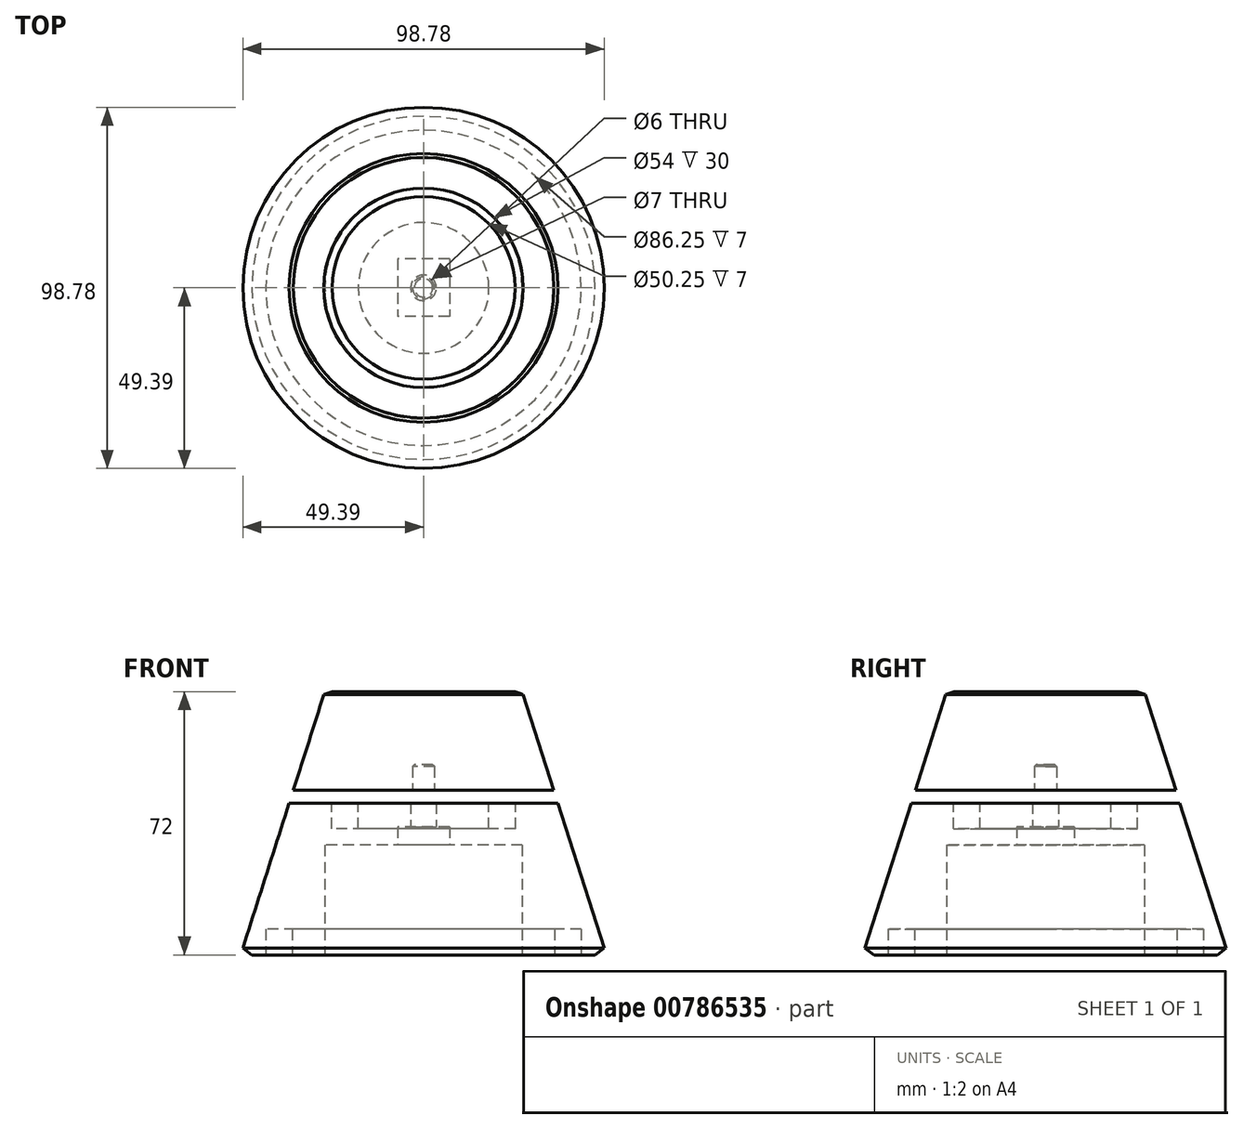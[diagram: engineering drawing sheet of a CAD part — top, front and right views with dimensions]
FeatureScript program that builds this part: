
annotation { "Feature Type Name" : "Feature", "Feature Type Description" : "" }
export const myFeature = defineFeature(function(context is Context, id is Id, definition is map)
    precondition{}
    {
        {
            var Q0;
            Q0=qCreatedBy(makeId("Top.planeOp"),FACE);
            var sketch = newSketch(context, id + "F0", { "sketchPlane" : qUnion([Q0])});
            skCircle(sketch, "E0", {"center": v(0, 0) * mm, "radius": 50 * mm});
            skSolve(sketch);
        }
        {
            var Q0;
            Q0 = qSketchRegion(id + "F0", true);
            extrude(context, id + "F1", {"entities" : qUnion([Q0]), "depth" : 72 * mm, "offsetDistance" : 25 * mm});
        }
        {
            var Q0;
            Q0=makeQuery(id+"F1.opExtrude","CAP_EDGE",EDGE,{"disambiguationData":[OSD([sQuery(id+"F0.wireOp",EDGE,"E0")])],"isStart":false});
            chamfer(context, id + "F2", {"entities" : qUnion([Q0]), "chamferType" : ChamferType.TWO_OFFSETS, "width1" : 23 * mm, "oppositeDirection" : false, "width2" : 72 * mm, "tangentPropagation" : true});
        }
        {
            var Q0;
            {var subQ0=sQuery(id+"F0.wireOp",EDGE,"E0");Q0=makeQuery(id+"F2.opChamfer","BLEND_EDGE",EDGE,{"blendedFrom":[makeQuery(id+"F1.opExtrude","CAP_EDGE",EDGE,{"disambiguationData":[OSD([subQ0])],"isStart":false}),makeQuery(id+"F1.opExtrude","CAP_FACE",FACE,{"disambiguationData":[OSD([subQ0])],"isStart":true})],"blendedInto":[makeQuery(id+"F1.opExtrude","CAP_FACE",FACE,{"disambiguationData":[OSD([subQ0])],"isStart":true})]});}
            chamfer(context, id + "F3", {"entities" : qUnion([Q0]), "chamferType" : ChamferType.OFFSET_ANGLE, "width" : 2 * mm, "oppositeDirection" : false, "angle" : 70 * degree, "tangentPropagation" : true});
        }
        {
            var Q0;
            {var subQ0=sQuery(id+"F0.wireOp",EDGE,"E0");Q0=makeQuery(id+"F2.opChamfer","BLEND_EDGE",EDGE,{"blendedFrom":[makeQuery(id+"F1.opExtrude","CAP_EDGE",EDGE,{"disambiguationData":[OSD([subQ0])],"isStart":false}),makeQuery(id+"F1.opExtrude","CAP_FACE",FACE,{"disambiguationData":[OSD([subQ0])],"isStart":false})],"blendedInto":[makeQuery(id+"F1.opExtrude","CAP_FACE",FACE,{"disambiguationData":[OSD([subQ0])],"isStart":false})]});}
            chamfer(context, id + "F4", {"entities" : qUnion([Q0]), "chamferType" : ChamferType.OFFSET_ANGLE, "width" : 2 * mm, "oppositeDirection" : false, "angle" : 20 * degree, "tangentPropagation" : true});
        }
        {
            var Q0;
            Q0=qCreatedBy(makeId("Top.planeOp"),FACE);
            var sketch = newSketch(context, id + "F5", { "sketchPlane" : qUnion([Q0])});
            skCircle(sketch, "E1", {"center": v(0, 0) * mm, "radius": 27 * mm});
            skSolve(sketch);
        }
        {
            var Q0;
            Q0 = qSketchRegion(id + "F5", true);
            extrude(context, id + "F6", {"entities" : qUnion([Q0]), "operationType" : NewBodyOperationType.REMOVE, "depth" : 30 * mm, "offsetDistance" : 25 * mm});
        }
        {
            var Q0;
            Q0=makeQuery(id+"F6.boolean.opBoolean","COPY",FACE,{"derivedFrom":makeQuery(id+"F6.opExtrude","CAP_FACE",FACE,{"disambiguationData":[OSD([sQuery(id+"F5.wireOp",EDGE,"E1")])],"isStart":false})});
            var sketch = newSketch(context, id + "F7", { "sketchPlane" : qUnion([Q0])});
            skLineSegment(sketch, "E2.bottom", {"start": v(7.12, -7.88) * mm, "end": v(-7.13, -7.88) * mm});
            skLineSegment(sketch, "E2.top", {"start": v(7.12, 7.88) * mm, "end": v(-7.12, 7.87) * mm});
            skLineSegment(sketch, "E2.left", {"start": v(7.12, -7.88) * mm, "end": v(7.12, 7.88) * mm});
            skLineSegment(sketch, "E2.right", {"start": v(-7.13, -7.88) * mm, "end": v(-7.12, 7.87) * mm});
            skPoint(sketch, "E2.middle", {"position": v(0, 0) * mm});
            skSolve(sketch);
        }
        {
            var Q0;
            Q0 = qSketchRegion(id + "F7", true);
            var Q1;
            Q1=sQuery(id+"F7.wireOp",EDGE,"nhaoerKo-kfoO-m88x-1wRI-986FIBOQnDxg");
            extrude(context, id + "F8", {"entities" : qUnion([Q0]), "operationType" : NewBodyOperationType.REMOVE, "surfaceEntities" : qUnion([Q1]), "oppositeDirection" : true, "depth" : 5 * mm, "offsetDistance" : 25 * mm});
        }
        {
            var Q0;
            Q0=makeQuery(id+"F5.imprint","IMPRINT",FACE,{"disambiguationData":[TD([[makeQuery(id+"F5.imprint","IMPRINT",EDGE,{"derivedFrom":sQuery(id+"F5.wireOp",EDGE,"E1")}),1.0]])]});
            var sketch = newSketch(context, id + "F9", { "sketchPlane" : qUnion([Q0])});
            skCircle(sketch, "E3", {"center": v(0, 0) * mm, "radius": 3.5 * mm});
            skSolve(sketch);
        }
        {
            var Q0;
            Q0 = qSketchRegion(id + "F9", true);
            extrude(context, id + "F10", {"entities" : qUnion([Q0]), "operationType" : NewBodyOperationType.REMOVE, "depth" : 41.5 * mm, "offsetDistance" : 25 * mm});
        }
        {
            var Q0;
            Q0=makeQuery(id+"F0.imprint","IMPRINT",FACE,{"disambiguationData":[TD([[makeQuery(id+"F0.imprint","IMPRINT",EDGE,{"derivedFrom":sQuery(id+"F0.wireOp",EDGE,"E0")}),1.0]])]});
            var sketch = newSketch(context, id + "F11", { "sketchPlane" : qUnion([Q0])});
            skCircle(sketch, "E4", {"center": v(0, 0) * mm, "radius": 3 * mm});
            skSolve(sketch);
        }
        {
            var Q0;
            Q0 = qSketchRegion(id + "F11", true);
            extrude(context, id + "F12", {"entities" : qUnion([Q0]), "operationType" : NewBodyOperationType.REMOVE, "depth" : 52 * mm, "offsetDistance" : 25 * mm});
        }
        {
            var Q0;
            Q0=makeQuery(id+"F12.boolean.opBoolean","COPY",EDGE,{"derivedFrom":makeQuery(id+"F12.opExtrude","CAP_EDGE",EDGE,{"disambiguationData":[OSD([sQuery(id+"F11.wireOp",EDGE,"E4")])],"isStart":false})});
            chamfer(context, id + "F13", {"entities" : qUnion([Q0]), "chamferType" : ChamferType.OFFSET_ANGLE, "width" : 0.5 * mm, "oppositeDirection" : false, "angle" : 45 * degree, "tangentPropagation" : true});
        }
        {
            var Q0;
            Q0=makeQuery(id+"F0.imprint","IMPRINT",FACE,{"disambiguationData":[TD([[makeQuery(id+"F0.imprint","IMPRINT",EDGE,{"derivedFrom":sQuery(id+"F0.wireOp",EDGE,"E0")}),1.0]])]});
            var sketch = newSketch(context, id + "F14", { "sketchPlane" : qUnion([Q0])});
            skCircle(sketch, "E5", {"center": v(0, 0) * mm, "radius": 35.88 * mm});
            skCircle(sketch, "E6", {"center": v(0, 0) * mm, "radius": 43.13 * mm});
            skSolve(sketch);
        }
        {
            var Q0;
            Q0 = qSketchRegion(id + "F14", true);
            var Q1;
            Q1=sQuery(id+"F14.wireOp",EDGE,"E6");
            var Q2;
            Q2=sQuery(id+"F14.wireOp",EDGE,"E5");
            extrude(context, id + "F15", {"entities" : qUnion([Q0]), "operationType" : NewBodyOperationType.REMOVE, "surfaceEntities" : qUnion([Q1, Q2]), "depth" : 7 * mm, "offsetDistance" : 25 * mm});
        }
        {
            var Q0;
            Q0=qCreatedBy(makeId("Front.planeOp"),FACE);
            var sketch = newSketch(context, id + "F16", { "sketchPlane" : qUnion([Q0])});
            skLineSegment(sketch, "E7", {"start": v(0, 90) * mm, "end": v(0, 0) * mm});
            skLineSegment(sketch, "E8.bottom", {"start": v(-37, 45) * mm, "end": v(37, 45) * mm});
            skLineSegment(sketch, "E8.top", {"start": v(-37, 41.5) * mm, "end": v(37, 41.5) * mm});
            skLineSegment(sketch, "E8.left", {"start": v(-37, 45) * mm, "end": v(-37, 41.5) * mm});
            skLineSegment(sketch, "E8.right", {"start": v(37, 45) * mm, "end": v(37, 41.5) * mm});
            skPoint(sketch, "E8.middle", {"position": v(0, 43.25) * mm});
            skPoint(sketch, "E8.cornerSnap0", {"position": v(0, 45) * mm});
            skLineSegment(sketch, "E9.bottom", {"start": v(25.12, 34.5) * mm, "end": v(17.88, 34.5) * mm});
            skLineSegment(sketch, "E9.top", {"start": v(25.12, 41.5) * mm, "end": v(17.88, 41.5) * mm});
            skLineSegment(sketch, "E9.left", {"start": v(25.12, 34.5) * mm, "end": v(25.12, 41.5) * mm});
            skLineSegment(sketch, "E9.right", {"start": v(17.88, 34.5) * mm, "end": v(17.88, 41.5) * mm});
            skPoint(sketch, "E9.middle", {"position": v(21.5, 38) * mm});
            skSolve(sketch);
        }
        {
            var Q0;
            {var subQ5=sQuery(id+"F16.wireOp",EDGE,"E8.left");Q0=makeQuery(id+"F16.imprint","IMPRINT",FACE,{"disambiguationData":[TD([[makeQuery(id+"F16.imprint","IMPRINT",EDGE,{"derivedFrom":subQ5}),1.0]])]});}
            var Q1;
            Q1=makeQuery(id+"F16.imprint","IMPRINT",FACE,{"disambiguationData":[TD([[makeQuery(id+"F16.imprint","IMPRINT",EDGE,{"derivedFrom":sQuery(id+"F16.wireOp",EDGE,"E9.bottom")}),-1.0]])]});
            var Q2;
            Q2=sQuery(id+"F16.wireOp",EDGE,"E7");
            revolve(context, id + "F17", {"operationType" : NewBodyOperationType.REMOVE, "surfaceOperationType" : NewSurfaceOperationType.NEW, "entities" : qUnion([Q0, Q1]), "axis" : qUnion([Q2]), "revolveType" : RevolveType.FULL});
        }
    });
